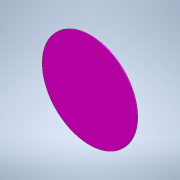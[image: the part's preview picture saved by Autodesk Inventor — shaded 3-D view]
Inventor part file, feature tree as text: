
AUTODESK INVENTOR PART (.ipt)
format: ipt  version: 2020.4 (Build 244396000, 396)  size: 93,696 bytes
history: native  units: mm
features: extrude x1, sketch x1
ambient origin geometry x8: Origin, YZ Plane, XZ Plane, XY Plane, X Axis, Y Axis, Z Axis, Center Point
bodies: Solid1 (feature_tree)
feature tree (2):
  extrude  "Extrusion1"  Depth=0.5mm TaperAngle=0.0deg
  sketch  "Sketch1"  dims[d0=45.0mm d1=0.5mm d2=0.0mm]
